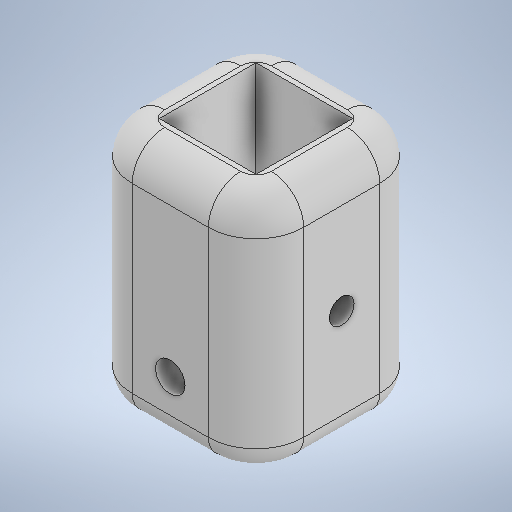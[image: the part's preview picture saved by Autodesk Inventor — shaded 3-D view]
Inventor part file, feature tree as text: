
AUTODESK INVENTOR PART (.ipt)
format: ipt  version: 2025 (Build 290162000, 162)  size: 298,496 bytes
history: native  units: in
note: dims shown in document units (in); Inventor stores cm internally (conversion verified against a paired STEP export)
features: sketch x5, extrude x3, fillet x3, hole x1
ambient origin geometry x8: Origin, YZ Plane, XZ Plane, XY Plane, X Axis, Y Axis, Z Axis, Center Point
bodies: Solid1 (feature_tree)
feature tree (12):
  extrude  "Extrusion1"  Depth=1.9685in
  extrude  "Extrusion2"  Depth=1.4173in
  hole  "Hole1"  [1 undecoded]
  sketch  "Sketch8"  dims[d7=1.2992in d8=0.0in d9=0.7087in d10=0.4724in]
  extrude  "Extrusion6"  Depth=1.2992in
  fillet  "Fillet1"  Radius=0.4724in
  fillet  "Fillet2"  Radius=0.2047in
  fillet  "Fillet3"  Radius=0.7087in
  sketch  "Sketch1"  dims[d0=1.4173in d1=1.9685in]
  sketch  "Sketch2"  dims[d2=1.4173in d3=0.0in d4=0.7087in]
  sketch  "Sketch3"  dims[d5=0.7992in d6=0.7992in]
  sketch  "Sketch11"  dims[d11=0.2441in d12=0.2362in d13=0.4921in d14=0.0669in d15=90.0deg d16=0.0709in d17=0.0in d41=0.2047in d42=0.7087in d43=0.2756in d44=0.3937in d45=0.0in d46=0.3937in d47=0.1969in d48=0.2677in d18=0.0295in d19=0.8108in d20=0.0025in d21=0.0295in d22=0.0148in d49=0.0394in d50=0.0059in d51=0.0098in d52=0.0148in d53=0.5635in d54=0.0295in d55=0.8108in d56=0.0025in d57=0.0295in d58=0.0148in]
note: 1 required parameter value undecoded (feature->parameter linkage not recoverable at this tier; creation-order binding heuristic only, values carry confidence <= 0.55)
